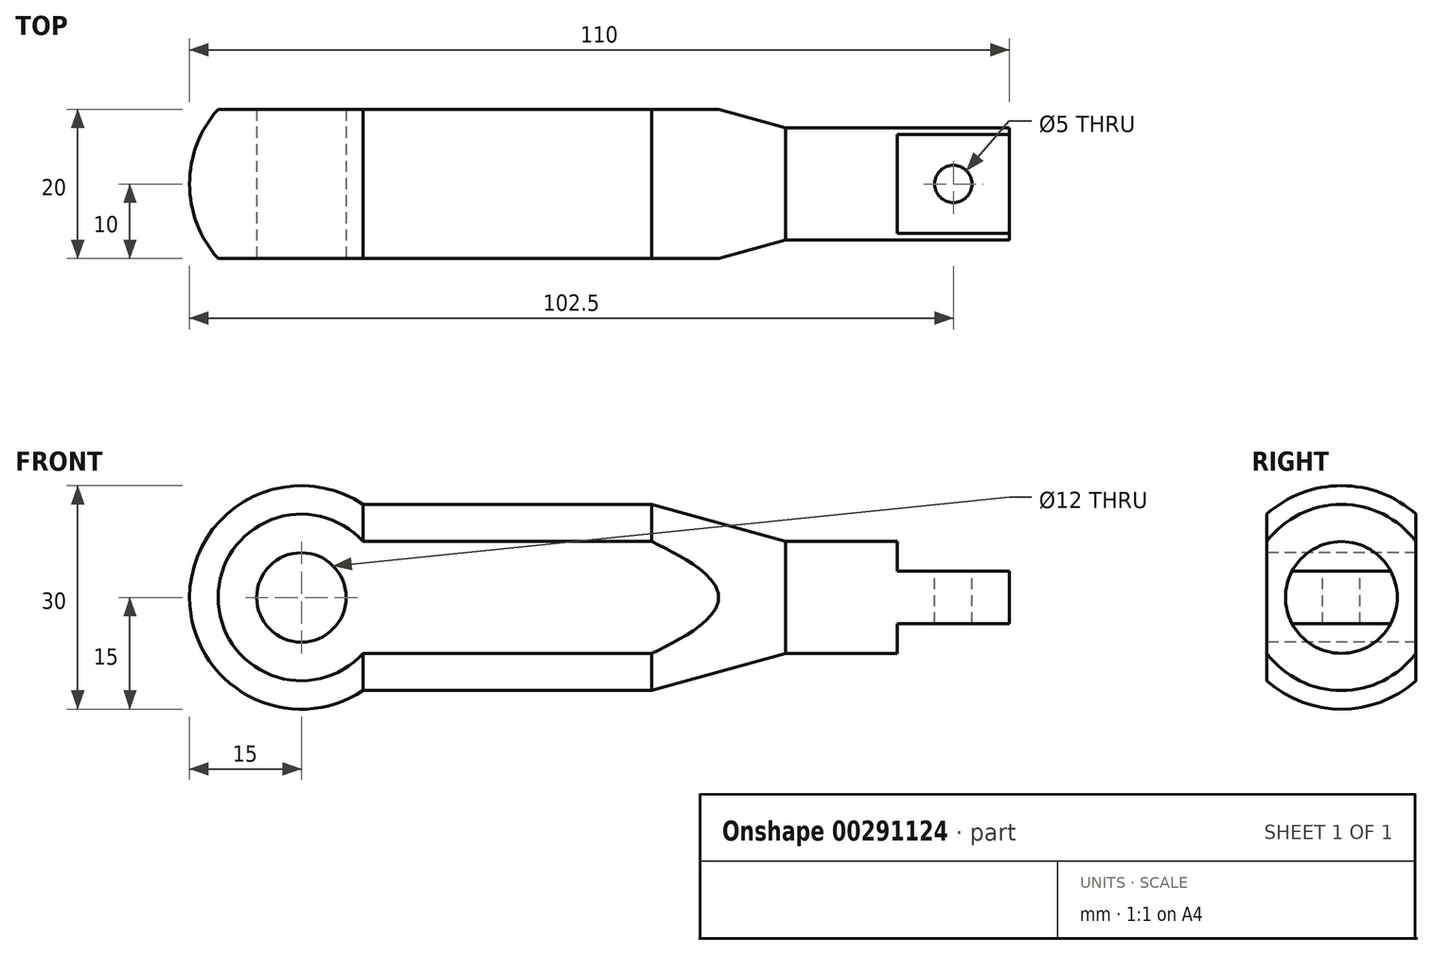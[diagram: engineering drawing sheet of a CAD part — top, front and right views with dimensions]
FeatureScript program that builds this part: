
annotation { "Feature Type Name" : "Feature", "Feature Type Description" : "" }
export const myFeature = defineFeature(function(context is Context, id is Id, definition is map)
    precondition{}
    {
        {
            var Q0;
            Q0=qCreatedBy(makeId("Front.planeOp"),FACE);
            var sketch = newSketch(context, id + "F0", { "sketchPlane" : qUnion([Q0])});
            skArc(sketch, "E0", {"start": v(-15, 0) * mm, "mid": v(-7.1, 13.22) * mm, "end": v(8.3, 12.5) * mm});
            skLineSegment(sketch, "E1", {"start": v(8.3, 12.5) * mm, "end": v(47, 12.5) * mm});
            skLineSegment(sketch, "E2", {"start": v(47, 12.5) * mm, "end": v(65, 7.5) * mm});
            skLineSegment(sketch, "E3", {"start": v(65, 7.5) * mm, "end": v(95, 7.5) * mm});
            skLineSegment(sketch, "E4", {"start": v(95, 7.5) * mm, "end": v(95, 0) * mm});
            skLineSegment(sketch, "E5", {"start": v(95, 0) * mm, "end": v(-15, 0) * mm});
            skLineSegment(sketch, "E6", {"start": v(118.46, 0) * mm, "end": v(-34.12, 0) * mm, "construction": true});
            skSolve(sketch);
        }
        {
            var Q0;
            Q0 = qSketchRegion(id + "F0", true);
            var Q1;
            Q1=sQuery(id+"F0.wireOp",EDGE,"E6");
            revolve(context, id + "F1", {"entities" : qUnion([Q0]), "axis" : qUnion([Q1]), "revolveType" : RevolveType.FULL});
        }
        {
            var Q0;
            Q0=qCreatedBy(makeId("Front.planeOp"),FACE);
            var sketch = newSketch(context, id + "F2", { "sketchPlane" : qUnion([Q0])});
            skLineSegment(sketch, "E7.bottom", {"start": v(80, 7.5) * mm, "end": v(95, 7.5) * mm});
            skLineSegment(sketch, "E7.right", {"start": v(95, 7.5) * mm, "end": v(95, 0) * mm});
            skLineSegment(sketch, "E8", {"start": v(80, 7.5) * mm, "end": v(80, 3.5) * mm});
            skLineSegment(sketch, "E9", {"start": v(80, 3.5) * mm, "end": v(95, 3.5) * mm});
            skLineSegment(sketch, "E10", {"start": v(95, 3.5) * mm, "end": v(95, 7.5) * mm});
            skLineSegment(sketch, "E11", {"start": v(119.19, 0) * mm, "end": v(-21.66, 0) * mm, "construction": true});
            skLineSegment(sketch, "E12.0", {"start": v(95, 7.5) * mm, "end": v(95, -7.5) * mm});
            skLineSegment(sketch, "E13.MirrorCS", {"start": v(80, -7.5) * mm, "end": v(95, -7.5) * mm});
            skLineSegment(sketch, "E14.MirrorCS", {"start": v(80, -3.5) * mm, "end": v(95, -3.5) * mm});
            skLineSegment(sketch, "E15.MirrorCS", {"start": v(95, -3.5) * mm, "end": v(95, -7.5) * mm});
            skLineSegment(sketch, "E16.MirrorCS", {"start": v(80, -7.5) * mm, "end": v(80, -3.5) * mm});
            skSolve(sketch);
        }
        {
            var Q0;
            Q0 = qSketchRegion(id + "F2", true);
            extrude(context, id + "F3", {"entities" : qUnion([Q0]), "operationType" : NewBodyOperationType.REMOVE, "endBound" : BoundingType.THROUGH_ALL, "oppositeDirection" : true, "depth" : 25.4 * mm});
        }
        {
            var Q0;
            Q0 = qSketchRegion(id + "F2", true);
            extrude(context, id + "F4", {"entities" : qUnion([Q0]), "operationType" : NewBodyOperationType.REMOVE, "endBound" : BoundingType.THROUGH_ALL, "depth" : 25.4 * mm});
        }
        {
            var Q0;
            {var subQ0=sQuery(id+"F2.wireOp",EDGE,"E9");Q0=makeQuery(id+"F4.boolean.opBoolean","MERGE",FACE,{"derivedFrom":[makeQuery(id+"F3.boolean.opBoolean","COPY",FACE,{"derivedFrom":makeQuery(id+"F3.opExtrude","SWEPT_FACE",FACE,{"disambiguationData":[OSD([subQ0])]})}),makeQuery(id+"F4.opExtrude","SWEPT_FACE",FACE,{"disambiguationData":[OSD([subQ0])]})]});}
            var sketch = newSketch(context, id + "F5", { "sketchPlane" : qUnion([Q0])});
            skCircle(sketch, "E17", {"center": v(87.5, 0) * mm, "radius": 2.5 * mm});
            skPoint(sketch, "E17.centerSnap0", {"position": v(87.5, 6.63) * mm});
            skSolve(sketch);
        }
        {
            var Q0;
            Q0 = qSketchRegion(id + "F5", true);
            extrude(context, id + "F6", {"entities" : qUnion([Q0]), "operationType" : NewBodyOperationType.REMOVE, "endBound" : BoundingType.THROUGH_ALL, "oppositeDirection" : true, "depth" : 25 * mm});
        }
        {
            var Q0;
            Q0=makeQuery(id+"F1.opRevolve","SWEPT_FACE",FACE,{"disambiguationData":[OSD([sQuery(id+"F0.wireOp",EDGE,"E4")])]});
            var sketch = newSketch(context, id + "F7", { "sketchPlane" : qUnion([Q0])});
            skLineSegment(sketch, "E18", {"start": v(-10, 11.18) * mm, "end": v(-10, -11.18) * mm});
            skLineSegment(sketch, "E19", {"start": v(10, 11.18) * mm, "end": v(10, -11.18) * mm});
            skArc(sketch, "E20", {"start": v(-10, 11.18) * mm, "mid": v(-15, 0) * mm, "end": v(-10, -11.18) * mm});
            skArc(sketch, "E21.trimOffspring", {"start": v(10, -11.18) * mm, "mid": v(15, 0) * mm, "end": v(10, 11.18) * mm});
            skSolve(sketch);
        }
        {
            var Q0;
            Q0 = qSketchRegion(id + "F7", true);
            extrude(context, id + "F8", {"entities" : qUnion([Q0]), "operationType" : NewBodyOperationType.REMOVE, "endBound" : BoundingType.THROUGH_ALL, "oppositeDirection" : true, "depth" : 25 * mm});
        }
        {
            var Q0;
            Q0=makeQuery(id+"F8.boolean.opBoolean","COPY",FACE,{"derivedFrom":makeQuery(id+"F8.opExtrude","SWEPT_FACE",FACE,{"disambiguationData":[OSD([sQuery(id+"F7.wireOp",EDGE,"E18")])]})});
            var sketch = newSketch(context, id + "F9", { "sketchPlane" : qUnion([Q0])});
            skCircle(sketch, "E22", {"center": v(0, 0) * mm, "radius": 6 * mm});
            skSolve(sketch);
        }
        {
            var Q0;
            Q0 = qSketchRegion(id + "F9", true);
            extrude(context, id + "F10", {"entities" : qUnion([Q0]), "operationType" : NewBodyOperationType.REMOVE, "endBound" : BoundingType.THROUGH_ALL, "oppositeDirection" : true, "depth" : 25 * mm});
        }
    });
